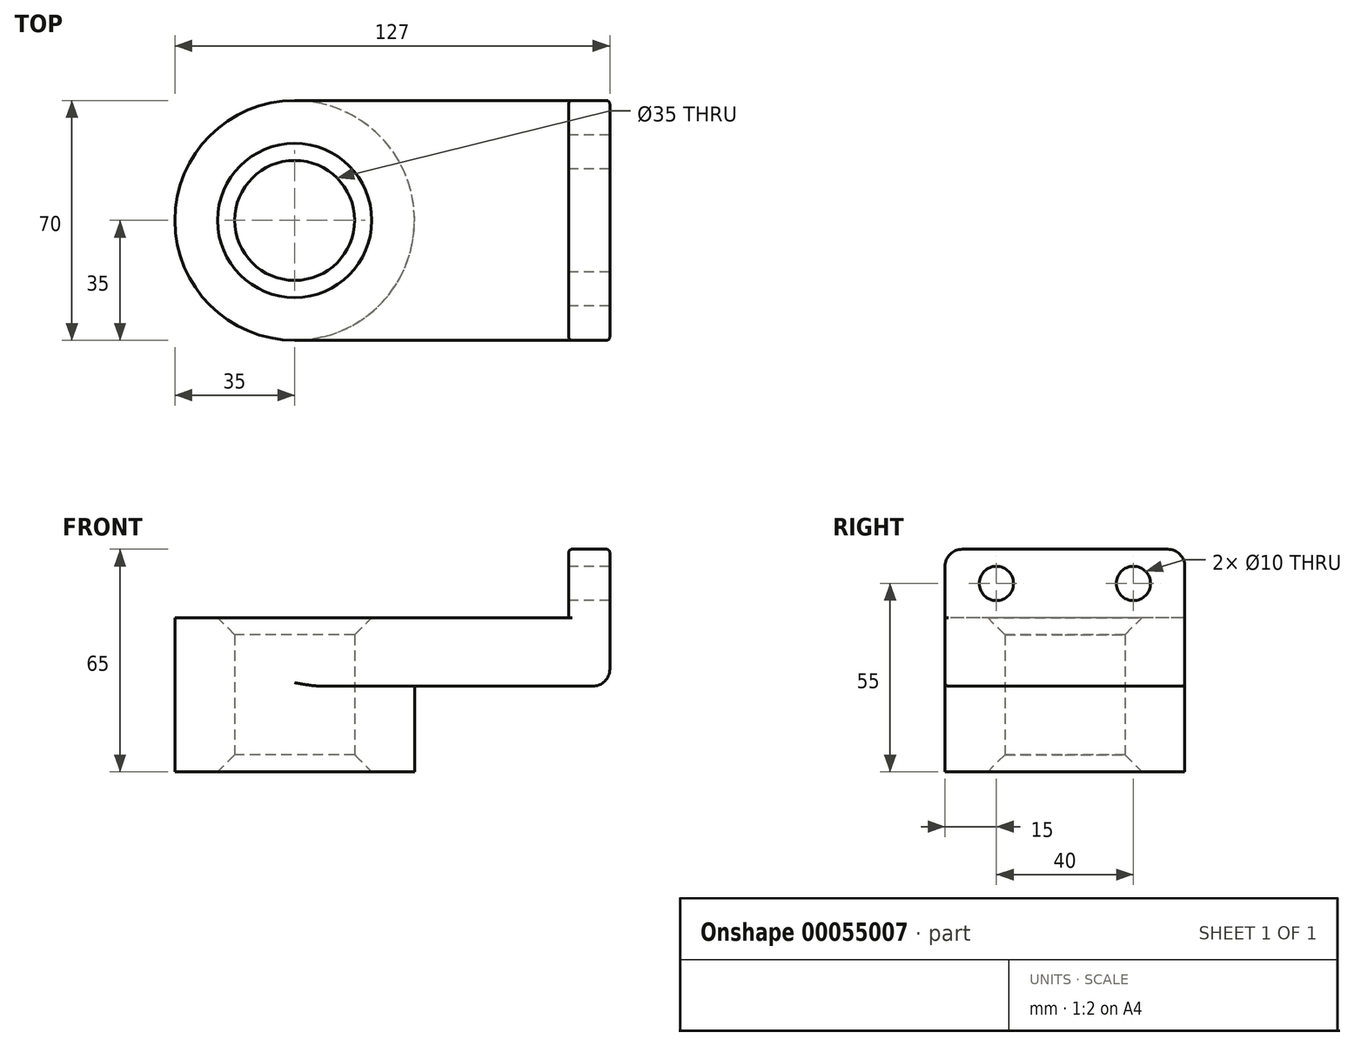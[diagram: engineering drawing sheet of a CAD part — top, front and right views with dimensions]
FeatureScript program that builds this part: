
annotation { "Feature Type Name" : "Feature", "Feature Type Description" : "" }
export const myFeature = defineFeature(function(context is Context, id is Id, definition is map)
    precondition{}
    {
        {
            var Q0;
            Q0=qCreatedBy(makeId("Top.planeOp"),FACE);
            var sketch = newSketch(context, id + "F0", { "sketchPlane" : qUnion([Q0])});
            skLineSegment(sketch, "E0.rect.bottom", {"start": v(40, 35) * mm, "end": v(-40, 35) * mm});
            skLineSegment(sketch, "E0.rect.top", {"start": v(40, -35) * mm, "end": v(-40, -35) * mm});
            skLineSegment(sketch, "E0.rect.left", {"start": v(40, 35) * mm, "end": v(40, -35) * mm});
            skLineSegment(sketch, "E0.rect.right", {"start": v(-40, 35) * mm, "end": v(-40, -35) * mm});
            skPoint(sketch, "E0.rect.middle", {"position": v(0, 0) * mm});
            skCircle(sketch, "E1", {"center": v(-40, 0) * mm, "radius": 35 * mm});
            skCircle(sketch, "E2", {"center": v(-40, 0) * mm, "radius": 17.5 * mm});
            skSolve(sketch);
        }
        {
            var Q0;
            {var subQ1=sQuery(id+"F0.wireOp",EDGE,"E0.rect.right");var subQ3=sQuery(id+"F0.wireOp",EDGE,"E2");var subQ4=makeQuery(id+"F0.imprint","INTERSECT",VERTEX,{"disambiguationData":[OD(0.0)],"derivedFrom":[subQ1,subQ3]});Q0=makeQuery(id+"F0.imprint","IMPRINT",FACE,{"disambiguationData":[TD([[makeQuery(id+"F0.imprint","IMPRINT",EDGE,{"disambiguationData":[TD([[subQ4,-1.0]])],"derivedFrom":subQ3}),-1.0]])]});}
            var Q1;
            {var subQ1=sQuery(id+"F0.wireOp",EDGE,"E0.rect.right");var subQ3=sQuery(id+"F0.wireOp",EDGE,"E2");var subQ4=makeQuery(id+"F0.imprint","INTERSECT",VERTEX,{"disambiguationData":[OD(0.0)],"derivedFrom":[subQ1,subQ3]});Q1=makeQuery(id+"F0.imprint","IMPRINT",FACE,{"disambiguationData":[TD([[makeQuery(id+"F0.imprint","IMPRINT",EDGE,{"disambiguationData":[TD([[subQ4,1.0]])],"derivedFrom":subQ3}),-1.0]])]});}
            var Q2;
            {var subQ0=sQuery(id+"F0.wireOp",EDGE,"E0.rect.bottom");Q2=makeQuery(id+"F0.imprint","IMPRINT",FACE,{"disambiguationData":[TD([[makeQuery(id+"F0.imprint","IMPRINT",EDGE,{"derivedFrom":subQ0}),1.0]])]});}
            extrude(context, id + "F1", {"entities" : qUnion([Q0, Q1, Q2]), "depth" : 20 * mm});
        }
        {
            var Q0;
            {var subQ1=sQuery(id+"F0.wireOp",EDGE,"E0.rect.right");var subQ3=sQuery(id+"F0.wireOp",EDGE,"E2");var subQ4=makeQuery(id+"F0.imprint","INTERSECT",VERTEX,{"disambiguationData":[OD(0.0)],"derivedFrom":[subQ1,subQ3]});Q0=makeQuery(id+"F0.imprint","IMPRINT",FACE,{"disambiguationData":[TD([[makeQuery(id+"F0.imprint","IMPRINT",EDGE,{"disambiguationData":[TD([[subQ4,1.0]])],"derivedFrom":subQ3}),-1.0]])]});}
            var Q1;
            {var subQ1=sQuery(id+"F0.wireOp",EDGE,"E0.rect.right");var subQ3=sQuery(id+"F0.wireOp",EDGE,"E2");var subQ4=makeQuery(id+"F0.imprint","INTERSECT",VERTEX,{"disambiguationData":[OD(0.0)],"derivedFrom":[subQ1,subQ3]});Q1=makeQuery(id+"F0.imprint","IMPRINT",FACE,{"disambiguationData":[TD([[makeQuery(id+"F0.imprint","IMPRINT",EDGE,{"disambiguationData":[TD([[subQ4,-1.0]])],"derivedFrom":subQ3}),-1.0]])]});}
            extrude(context, id + "F2", {"entities" : qUnion([Q0, Q1]), "operationType" : NewBodyOperationType.ADD, "oppositeDirection" : true, "depth" : 25 * mm});
        }
        {
            var Q0;
            Q0=makeQuery(id+"F1.opExtrude","SWEPT_FACE",FACE,{"disambiguationData":[OSD([sQuery(id+"F0.wireOp",EDGE,"E0.rect.left")])]});
            var sketch = newSketch(context, id + "F3", { "sketchPlane" : qUnion([Q0])});
            skLineSegment(sketch, "E3.bottom", {"start": v(35, 0) * mm, "end": v(-35, 0) * mm});
            skLineSegment(sketch, "E3.top", {"start": v(35, 40) * mm, "end": v(-35, 40) * mm});
            skLineSegment(sketch, "E3.left", {"start": v(35, 0) * mm, "end": v(35, 40) * mm});
            skLineSegment(sketch, "E3.right", {"start": v(-35, 0) * mm, "end": v(-35, 40) * mm});
            skCircle(sketch, "E4", {"center": v(20, 30) * mm, "radius": 5 * mm});
            skLineSegment(sketch, "E5", {"start": v(0, 40) * mm, "end": v(0, -32.88) * mm, "construction": true});
            skPoint(sketch, "E5.endSnap0", {"position": v(0, 20) * mm});
            skCircle(sketch, "E6.MirrorC", {"center": v(-20, 30) * mm, "radius": 5 * mm});
            skSolve(sketch);
        }
        {
            var Q0;
            {var subQ0=sQuery(id+"F3.wireOp",EDGE,"E3.bottom");Q0=makeQuery(id+"F3.imprint","IMPRINT",FACE,{"disambiguationData":[TD([[makeQuery(id+"F3.imprint","IMPRINT",EDGE,{"derivedFrom":subQ0}),-1.0]])]});}
            var Q1;
            {var subQ2=sQuery(id+"F3.wireOp",EDGE,"E3.top");Q1=makeQuery(id+"F3.imprint","IMPRINT",FACE,{"disambiguationData":[TD([[makeQuery(id+"F3.imprint","IMPRINT",EDGE,{"derivedFrom":subQ2}),1.0]])]});}
            extrude(context, id + "F4", {"entities" : qUnion([Q0, Q1]), "operationType" : NewBodyOperationType.ADD, "depth" : 12 * mm});
        }
        {
            var Q0;
            Q0=makeQuery(id+"F2.opExtrude","CAP_EDGE",EDGE,{"disambiguationData":[OSD([sQuery(id+"F0.wireOp",EDGE,"E1")])],"isStart":true});
            var Q1;
            Q1=makeQuery(id+"F4.opExtrude","CAP_EDGE",EDGE,{"disambiguationData":[OSD([sQuery(id+"F3.wireOp",EDGE,"E3.bottom")])],"isStart":false});
            var Q2;
            Q2=makeQuery(id+"F4.opExtrude","SWEPT_EDGE",EDGE,{"disambiguationData":[OSD([sQuery(id+"F3.wireOp",EDGE,"E3.top"),sQuery(id+"F3.wireOp",EDGE,"E3.left")])]});
            var Q3;
            Q3=makeQuery(id+"F4.opExtrude","SWEPT_EDGE",EDGE,{"disambiguationData":[OSD([sQuery(id+"F3.wireOp",EDGE,"E3.top"),sQuery(id+"F3.wireOp",EDGE,"E3.right")])]});
            fillet(context, id + "F5", {"entities" : qUnion([Q0, Q1, Q2, Q3]), "radius" : 5 * mm, "tangentPropagation" : true, "allowEdgeOverflow" : false});
        }
        {
            var Q0;
            {var subQ0=sQuery(id+"F0.wireOp",EDGE,"E2");Q0=makeQuery(id+"F2.boolean.opBoolean","MERGE",FACE,{"derivedFrom":[makeQuery(id+"F1.opExtrude","SWEPT_FACE",FACE,{"disambiguationData":[OSD([subQ0])]}),makeQuery(id+"F2.opExtrude","SWEPT_FACE",FACE,{"disambiguationData":[OSD([subQ0])]})]});}
            chamfer(context, id + "F6", {"entities" : qUnion([Q0]), "width" : 5 * mm, "tangentPropagation" : true});
        }
        {
            var Q0;
            Q0=makeQuery(id+"F4.opExtrude","CAP_EDGE",EDGE,{"disambiguationData":[OSD([sQuery(id+"F3.wireOp",EDGE,"E3.top")])],"isStart":true});
            var Q1;
            Q1=makeQuery(id+"F4.opExtrude","CAP_EDGE",EDGE,{"disambiguationData":[OSD([sQuery(id+"F3.wireOp",EDGE,"E3.top")])],"isStart":false});
            var Q2;
            Q2=makeQuery(id+"F1.opExtrude","CAP_EDGE",EDGE,{"disambiguationData":[OSD([sQuery(id+"F0.wireOp",EDGE,"E0.rect.left")])],"isStart":false});
            fillet(context, id + "F7", {"entities" : qUnion([Q0, Q1, Q2]), "radius" : 1 * mm, "tangentPropagation" : true, "allowEdgeOverflow" : false});
        }
    });
